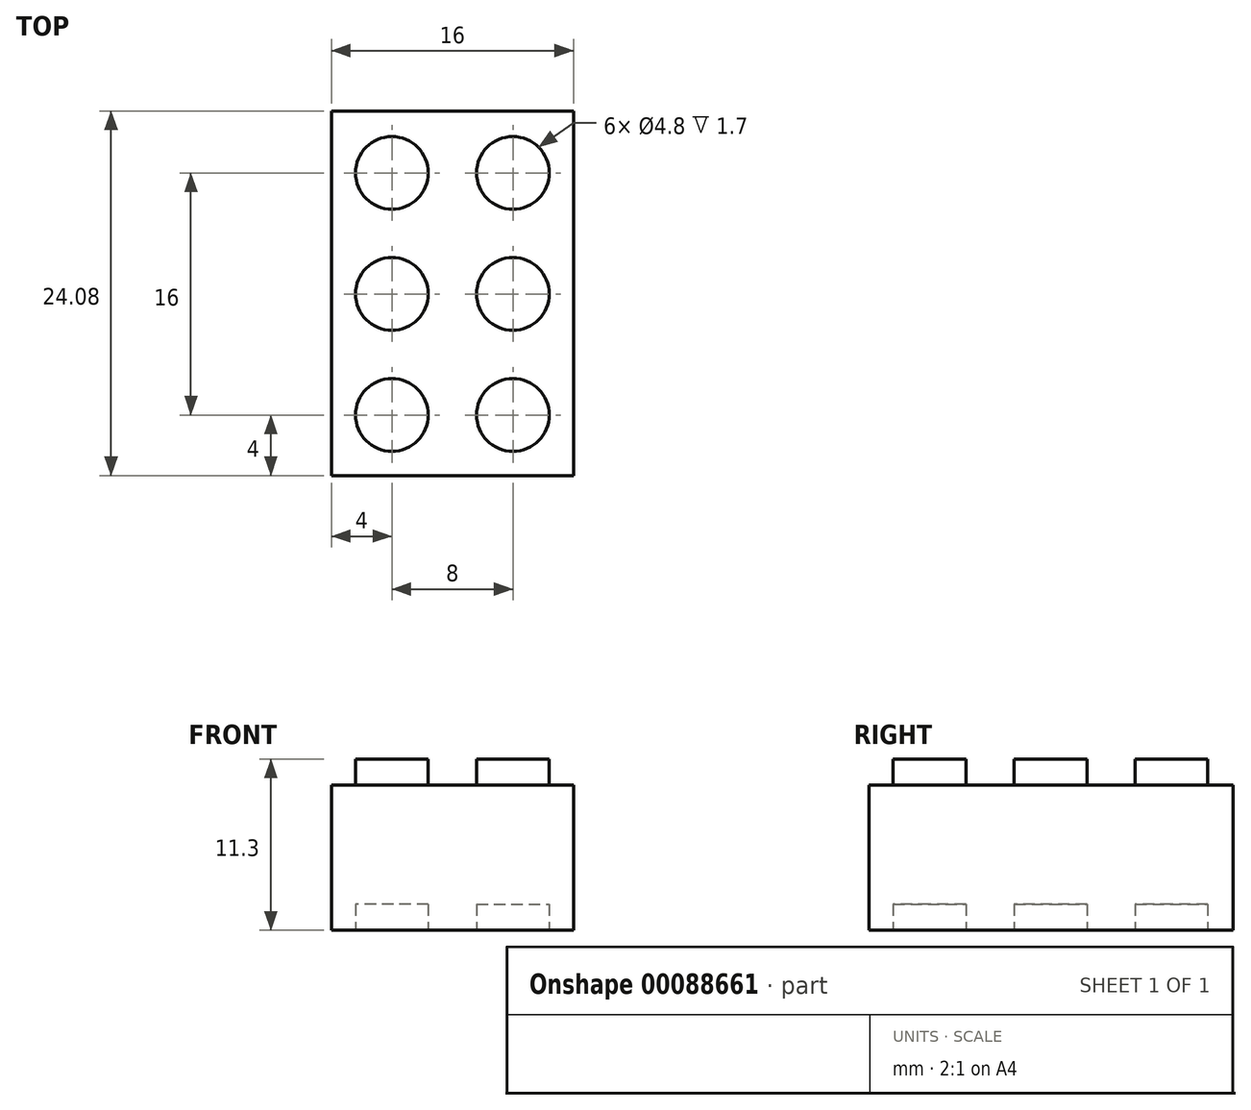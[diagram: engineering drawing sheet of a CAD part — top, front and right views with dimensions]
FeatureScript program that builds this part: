
annotation { "Feature Type Name" : "Feature", "Feature Type Description" : "" }
export const myFeature = defineFeature(function(context is Context, id is Id, definition is map)
    precondition{}
    {
        {
            var Q0;
            Q0=qCreatedBy(makeId("Front.planeOp"),FACE);
            var sketch = newSketch(context, id + "F0", { "sketchPlane" : qUnion([Q0])});
            skLineSegment(sketch, "E0.bottom", {"start": v(-4, 9.6) * mm, "end": v(-2.4, 9.6) * mm});
            skLineSegment(sketch, "E0.top", {"start": v(-4, 0) * mm, "end": v(4, 0) * mm});
            skLineSegment(sketch, "E0.left", {"start": v(-4, 9.6) * mm, "end": v(-4, 0) * mm});
            skLineSegment(sketch, "E0.right", {"start": v(4, 9.6) * mm, "end": v(4, 0) * mm});
            skLineSegment(sketch, "E1.top", {"start": v(-2.4, 11.3) * mm, "end": v(2.4, 11.3) * mm});
            skLineSegment(sketch, "E1.left", {"start": v(-2.4, 9.6) * mm, "end": v(-2.4, 11.3) * mm});
            skLineSegment(sketch, "E1.right", {"start": v(2.4, 9.6) * mm, "end": v(2.4, 11.3) * mm});
            skLineSegment(sketch, "E2", {"start": v(0, 0) * mm, "end": v(0, 24.04) * mm, "construction": true});
            skLineSegment(sketch, "E3.trimOffspring", {"start": v(2.4, 9.6) * mm, "end": v(4, 9.6) * mm});
            skSolve(sketch);
        }
        {
            var Q0;
            Q0=makeQuery(id+"F0.imprint","IMPRINT",FACE,{"disambiguationData":[TD([[makeQuery(id+"F0.imprint","IMPRINT",EDGE,{"derivedFrom":sQuery(id+"F0.wireOp",EDGE,"E0.bottom")}),-1.0]])]});
            extrude(context, id + "F1", {"entities" : qUnion([Q0]), "depth" : 8 * mm});
        }
        {
            var Q0;
            Q0=qCreatedBy(makeId("Top.planeOp"),FACE);
            var Q1;
            Q1=makeQuery(id+"F1.opExtrude","CAP_VERTEX",VERTEX,{"disambiguationData":[OSD([sQuery(id+"F0.wireOp",EDGE,"E1.top"),sQuery(id+"F0.wireOp",EDGE,"E1.right")])],"isStart":true});
            cPlane(context, id + "F2", {"entities" : qUnion([Q0, Q1]), "cplaneType" : CPlaneType.PLANE_POINT, "offset" : 152.4 * mm, "width" : 152.4 * mm, "height" : 152.4 * mm});
        }
        {
            var Q0;
            Q0=qCreatedBy(id+"F2.planeOp",FACE);
            var sketch = newSketch(context, id + "F3", { "sketchPlane" : qUnion([Q0])});
            skLineSegment(sketch, "E4.0", {"start": v(-4, -8) * mm, "end": v(-4, 0) * mm});
            skLineSegment(sketch, "E5.0", {"start": v(4, -8) * mm, "end": v(4, 0) * mm});
            skLineSegment(sketch, "E6", {"start": v(-4, 0) * mm, "end": v(4, 0) * mm});
            skLineSegment(sketch, "E7", {"start": v(-4, -8) * mm, "end": v(4, -8) * mm});
            skLineSegment(sketch, "E8", {"start": v(-4, 0) * mm, "end": v(4, -8) * mm, "construction": true});
            skLineSegment(sketch, "E9", {"start": v(-4, -8) * mm, "end": v(4, 0) * mm, "construction": true});
            skCircle(sketch, "E10", {"center": v(0, -4) * mm, "radius": 2.4 * mm});
            skSolve(sketch);
        }
        {
            var Q0;
            Q0=qSketchRegion(id+"F3",true);
            var Q1;
            Q1=makeQuery(id+"F1.opExtrude","SWEPT_FACE",FACE,{"disambiguationData":[OSD([sQuery(id+"F0.wireOp",EDGE,"E0.bottom")])]});
            extrude(context, id + "F4", {"entities" : qUnion([Q0]), "operationType" : NewBodyOperationType.REMOVE, "endBound" : BoundingType.UP_TO_SURFACE, "oppositeDirection" : true, "endBoundEntityFace" : qUnion([Q1]), "depth" : 25.4 * mm});
        }
        {
            var Q0;
            Q0=qCreatedBy(makeId("Top.planeOp"),FACE);
            var sketch = newSketch(context, id + "F5", { "sketchPlane" : qUnion([Q0])});
            skCircle(sketch, "E11.0", {"center": v(0, -4) * mm, "radius": 2.4 * mm});
            skSolve(sketch);
        }
        {
            var Q0;
            Q0=makeQuery(id+"F5.imprint","IMPRINT",FACE,{"disambiguationData":[TD([[makeQuery(id+"F5.imprint","IMPRINT",EDGE,{"derivedFrom":sQuery(id+"F5.wireOp",EDGE,"E11.0")}),1.0]])]});
            extrude(context, id + "F6", {"entities" : qUnion([Q0]), "operationType" : NewBodyOperationType.REMOVE, "depth" : 1.7 * mm});
        }
        {
            var Q0;
            Q0=qCreatedBy(makeId("Right.planeOp"),FACE);
            var Q1;
            Q1=makeQuery(id+"F1.opExtrude","CAP_VERTEX",VERTEX,{"disambiguationData":[OSD([sQuery(id+"F0.wireOp",EDGE,"E0.right"),sQuery(id+"F0.wireOp",EDGE,"E3.trimOffspring")])],"isStart":false});
            cPlane(context, id + "F7", {"entities" : qUnion([Q0, Q1]), "cplaneType" : CPlaneType.PLANE_POINT, "offset" : 152.4 * mm, "width" : 152.4 * mm, "height" : 152.4 * mm});
        }
        {
            var Q0;
            Q0=makeQuery(id+"F1.opExtrude","SWEPT_BODY",BODY,{"disambiguationData":[OSD([sQuery(id+"F0.wireOp",EDGE,"E0.bottom"),sQuery(id+"F0.wireOp",EDGE,"E0.top"),sQuery(id+"F0.wireOp",EDGE,"E0.left"),sQuery(id+"F0.wireOp",EDGE,"E0.right"),sQuery(id+"F0.wireOp",EDGE,"E1.top"),sQuery(id+"F0.wireOp",EDGE,"E1.left"),sQuery(id+"F0.wireOp",EDGE,"E1.right"),sQuery(id+"F0.wireOp",EDGE,"E3.trimOffspring")])]});
            var Q1;
            Q1=qCreatedBy(id+"F7.planeOp",FACE);
            mirror(context, id + "F8", {"operationType" : NewBodyOperationType.ADD, "entities" : qUnion([Q0]), "mirrorPlane" : qUnion([Q1])});
        }
        {
            var Q0;
            Q0=makeQuery(id+"F1.opExtrude","SWEPT_BODY",BODY,{"disambiguationData":[OSD([sQuery(id+"F0.wireOp",EDGE,"E0.bottom"),sQuery(id+"F0.wireOp",EDGE,"E0.top"),sQuery(id+"F0.wireOp",EDGE,"E0.left"),sQuery(id+"F0.wireOp",EDGE,"E0.right"),sQuery(id+"F0.wireOp",EDGE,"E1.top"),sQuery(id+"F0.wireOp",EDGE,"E1.left"),sQuery(id+"F0.wireOp",EDGE,"E1.right"),sQuery(id+"F0.wireOp",EDGE,"E3.trimOffspring")])]});
            var Q1;
            {var subQ0=makeQuery(id+"F1.opExtrude","CAP_FACE",FACE,{"disambiguationData":[OSD([sQuery(id+"F0.wireOp",EDGE,"E0.bottom"),sQuery(id+"F0.wireOp",EDGE,"E0.top"),sQuery(id+"F0.wireOp",EDGE,"E0.left"),sQuery(id+"F0.wireOp",EDGE,"E0.right"),sQuery(id+"F0.wireOp",EDGE,"E1.top"),sQuery(id+"F0.wireOp",EDGE,"E1.left"),sQuery(id+"F0.wireOp",EDGE,"E1.right"),sQuery(id+"F0.wireOp",EDGE,"E3.trimOffspring")])],"isStart":false});Q1=makeQuery(id+"F8.boolean.opBoolean","MERGE",FACE,{"derivedFrom":[subQ0,makeQuery(id+"F8.opPattern","COPY",FACE,{"derivedFrom":subQ0,"instanceName":"1"})]});}
            mirror(context, id + "F9", {"operationType" : NewBodyOperationType.ADD, "entities" : qUnion([Q0]), "mirrorPlane" : qUnion([Q1])});
        }
        {
            var Q0;
            Q0=makeQuery(id+"F1.opExtrude","SWEPT_BODY",BODY,{"disambiguationData":[OSD([sQuery(id+"F0.wireOp",EDGE,"E0.bottom"),sQuery(id+"F0.wireOp",EDGE,"E0.top"),sQuery(id+"F0.wireOp",EDGE,"E0.left"),sQuery(id+"F0.wireOp",EDGE,"E0.right"),sQuery(id+"F0.wireOp",EDGE,"E1.top"),sQuery(id+"F0.wireOp",EDGE,"E1.left"),sQuery(id+"F0.wireOp",EDGE,"E1.right"),sQuery(id+"F0.wireOp",EDGE,"E3.trimOffspring")])]});
            var Q1;
            {var subQ0=makeQuery(id+"F1.opExtrude","CAP_FACE",FACE,{"disambiguationData":[OSD([sQuery(id+"F0.wireOp",EDGE,"E0.bottom"),sQuery(id+"F0.wireOp",EDGE,"E0.top"),sQuery(id+"F0.wireOp",EDGE,"E0.left"),sQuery(id+"F0.wireOp",EDGE,"E0.right"),sQuery(id+"F0.wireOp",EDGE,"E1.top"),sQuery(id+"F0.wireOp",EDGE,"E1.left"),sQuery(id+"F0.wireOp",EDGE,"E1.right"),sQuery(id+"F0.wireOp",EDGE,"E3.trimOffspring")])],"isStart":true});Q1=makeQuery(id+"F9.opPattern","COPY",FACE,{"derivedFrom":makeQuery(id+"F8.boolean.opBoolean","MERGE",FACE,{"derivedFrom":[subQ0,makeQuery(id+"F8.opPattern","COPY",FACE,{"derivedFrom":subQ0,"instanceName":"1"})]}),"instanceName":"1"});}
            mirror(context, id + "F10", {"operationType" : NewBodyOperationType.ADD, "entities" : qUnion([Q0]), "mirrorPlane" : qUnion([Q1])});
        }
        {
            var Q0;
            Q0=qCreatedBy(makeId("Front.planeOp"),FACE);
            var sketch = newSketch(context, id + "F11", { "sketchPlane" : qUnion([Q0])});
            skLineSegment(sketch, "E12.bottom", {"start": v(-12.2, 12.7) * mm, "end": v(18.85, 12.7) * mm});
            skLineSegment(sketch, "E12.top", {"start": v(-12.2, -12.7) * mm, "end": v(18.85, -12.7) * mm});
            skLineSegment(sketch, "E12.left", {"start": v(-12.2, 12.7) * mm, "end": v(-12.2, -12.7) * mm});
            skLineSegment(sketch, "E12.right", {"start": v(18.85, 12.7) * mm, "end": v(18.85, -12.7) * mm});
            skPoint(sketch, "E12.middle", {"position": v(3.33, 0) * mm});
            skSolve(sketch);
        }
        {
            var Q0;
            Q0=makeQuery(id+"F11.imprint","IMPRINT",FACE,{"disambiguationData":[TD([[makeQuery(id+"F11.imprint","IMPRINT",EDGE,{"derivedFrom":sQuery(id+"F11.wireOp",EDGE,"E12.bottom")}),-1.0]])]});
            extrude(context, id + "F12", {"entities" : qUnion([Q0]), "operationType" : NewBodyOperationType.REMOVE, "depth" : 7.92 * mm, "offsetDistance" : 25.4 * mm});
        }
    });
